# Revit family: Sanitary_Other_Encon-Safety_Supply-Pipe-Mount-Eye-Facewash-Yello-Bowl
name_source: partatom
category: Plumbing Fixtures
units: mm (PartAtom-declared; Revit-internal decimal feet)

## family parameters
Always vertical = Yes
Cut with Voids When Loaded = No
OmniClass Number = 23.45.05.14.24
OmniClass Title = Eye Wash Fountains
Part Type = Normal
Room Calculation Point = No
Round Connector Dimension = Use Diameter
Shared = No
Work Plane-Based = No

## types (1)
- 01035401
    Assembly Code = D2010600
    Bowl Material = Encon Safety Products - Plastic - ABS - Yellow
    CW Connection = Yes
    CWFU = 0
    Description = Supply Pipe Mount Eye/Facewash Yello-Bowl®, 8.0 gpm ABS Facewash Heads
    Drain Type = slip joint tailpiece
    Edition number = 1
    Flow = 8 GPM
    Fluid out Diameter = 1 1/2"
    HW Connection = No
    HWFU = 0
    Heads Material = Encon Safety Products - Plastic - Acetal - Yellow
    Height = 10"
    Keynote = 15410
    Manufacturer = Encon Safety Products
    Model = 01035401
    Pedestal Material = Encon Safety Products - Metal - Stainless Steel
    Piping Material = Encon Safety Products - Plastic - PVC - Black
    Product Guid = a9e1b66d-2297-400b-9eb1-f3def4c2ea32
    Product data url = https://www.bimobject.com
    Supply Diameter = 1/2"
    URL = https://enconsafety.com
    Vent Connection = No
    WFU = 0
    Waste Connection = Yes
    Width = 11"

## geometry (parser evidence)
native form markers: Sweep x2
no freeform markers — native parametric forms only
